# Revit family: Arper_Aava-02_stool_bar_4woodlegs_wood_7631
name_source: partatom
category: Furniture
units: mm (PartAtom-declared; Revit-internal decimal feet)

## family parameters
Always vertical = Yes
Cut with Voids When Loaded = No
OmniClass Number = 23.40.20.00
OmniClass Title = General Furniture and Specialties
Room Calculation Point = No
Shared = No
Work Plane-Based = No

## types (1)
- Arper_Aava-02_stool_bar_4woodlegs_wood_7631
    Arper - Legs material = Arper - L0028
    Default Elevation = 0 mm  [stored 0 ft]
    Description = Stool on a 4-leg base and shell in plywood with a reconstituted oak 
or walnut finish. Base and shell can be configured in the same finish, 
or by combining various wood finishes. Glides are also available, 
with felt insert for wood floors. Seat height 76 cm.
    Manufacturer = ARPER s.p.a.
    Model = Aava 02
    URL = http://www.arper.com

note: [stored X ft] marks values corroborated as IEEE doubles in the binary element streams (Revit-internal decimal feet)
